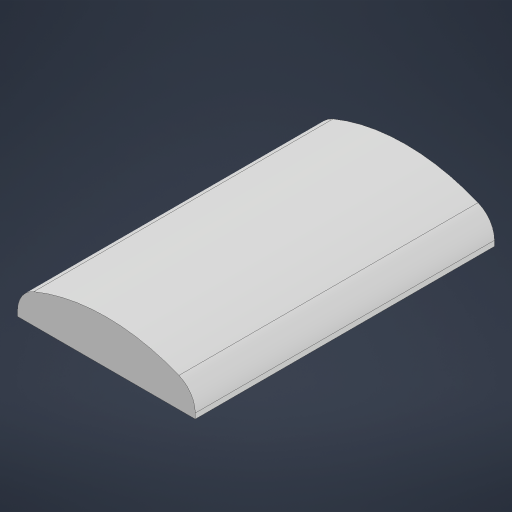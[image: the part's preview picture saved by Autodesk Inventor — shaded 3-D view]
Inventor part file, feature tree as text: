
AUTODESK INVENTOR PART (.ipt)
format: ipt  version: 2023 (Build 270158000, 158)  size: 175,104 bytes
history: native  units: in
note: dims shown in document units (in); Inventor stores cm internally (conversion verified against a paired STEP export)
features: extrude x2, sketch x2, fillet x1
ambient origin geometry x8: Origin, YZ Plane, XZ Plane, XY Plane, X Axis, Y Axis, Z Axis, Center Point
bodies: Solid1 (feature_tree)
feature tree (5):
  extrude  "Extrusion1"  Depth=0.6693in
  extrude  "Extrusion2"  Depth=0.0591in TaperAngle=0.0deg
  fillet  "Fillet1"  Radius=0.0591in
  sketch  "Sketch1"  dims[d0=0.3976in d1=0.6693in]
  sketch  "Sketch2"  dims[d2=0.0984in d3=0.0in d4=0.7141in d5=0.0in d6=0.0591in]
